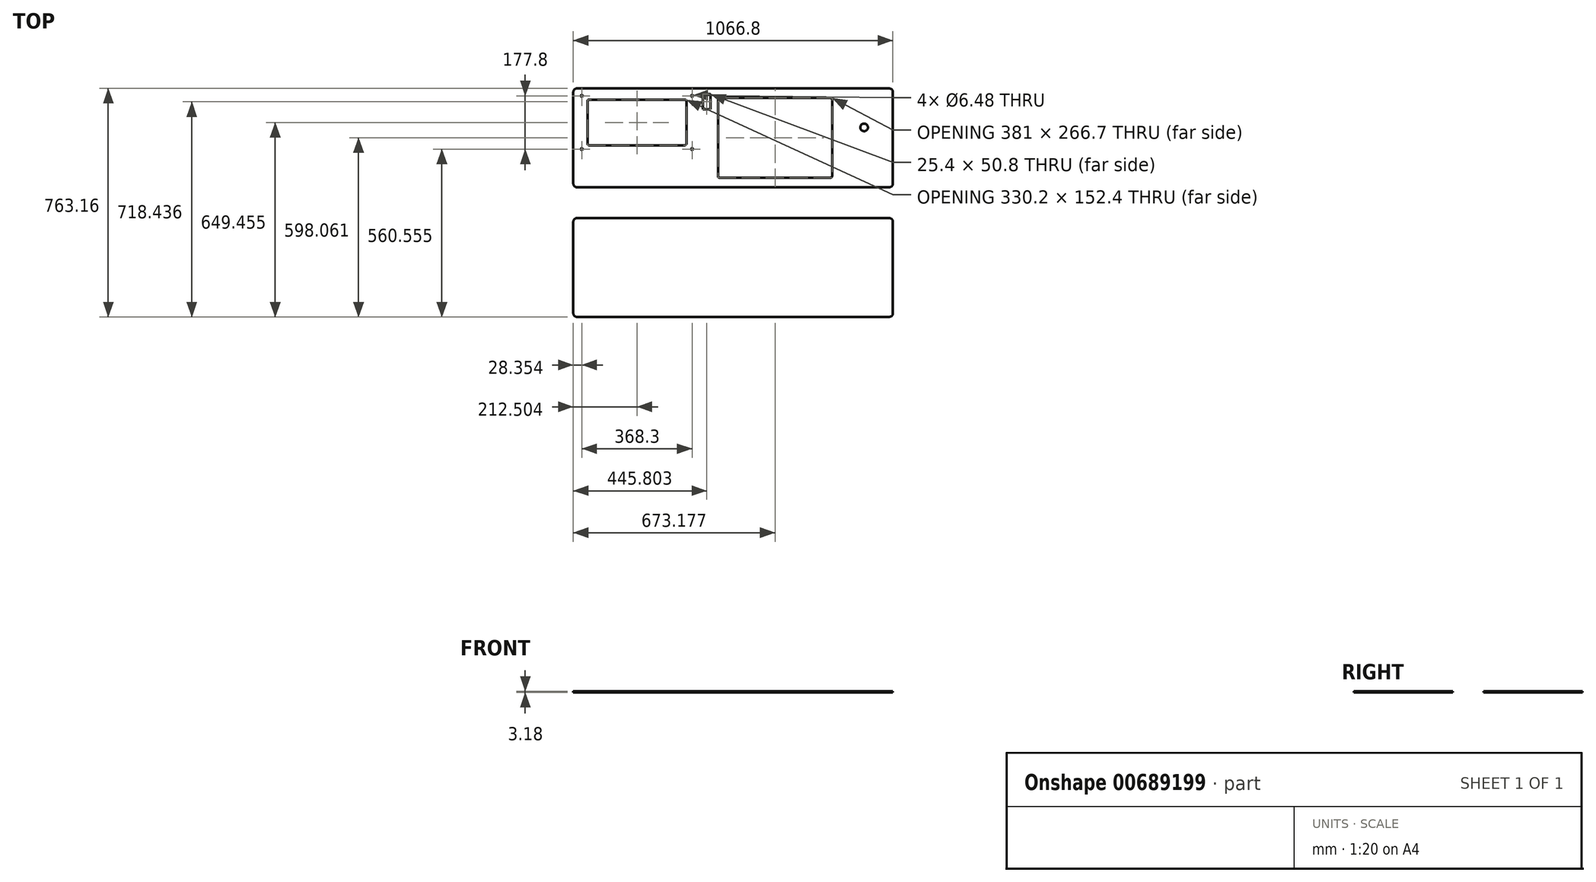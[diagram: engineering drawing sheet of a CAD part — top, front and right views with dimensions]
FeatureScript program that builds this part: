
annotation { "Feature Type Name" : "Feature", "Feature Type Description" : "" }
export const myFeature = defineFeature(function(context is Context, id is Id, definition is map)
    precondition{}
    {
        {
            var Q0;
            Q0=qCreatedBy(makeId("Top.planeOp"),FACE);
            var sketch = newSketch(context, id + "F0", { "sketchPlane" : qUnion([Q0])});
            skLineSegment(sketch, "E0.bottom", {"start": v(-578.64, 150) * mm, "end": v(488.16, 150) * mm});
            skLineSegment(sketch, "E0.top", {"start": v(-578.64, -180.2) * mm, "end": v(488.16, -180.2) * mm});
            skLineSegment(sketch, "E0.left", {"start": v(-578.64, 150) * mm, "end": v(-578.64, -180.2) * mm});
            skLineSegment(sketch, "E0.right", {"start": v(488.16, 150) * mm, "end": v(488.16, -180.2) * mm});
            skPoint(sketch, "E0.middle", {"position": v(-45.24, -15.1) * mm});
            skLineSegment(sketch, "E1.bottom", {"start": v(-95.96, -148.46) * mm, "end": v(285.04, -148.46) * mm});
            skLineSegment(sketch, "E1.top", {"start": v(-95.96, 118.24) * mm, "end": v(285.04, 118.24) * mm});
            skLineSegment(sketch, "E1.left", {"start": v(-95.96, -148.46) * mm, "end": v(-95.96, 118.24) * mm});
            skLineSegment(sketch, "E1.right", {"start": v(285.04, -148.46) * mm, "end": v(285.04, 118.24) * mm});
            skPoint(sketch, "E1.middle", {"position": v(94.54, -15.1) * mm});
            skLineSegment(sketch, "E2.bottom", {"start": v(-531.24, 112.49) * mm, "end": v(-201.04, 112.49) * mm});
            skLineSegment(sketch, "E2.top", {"start": v(-531.24, -39.91) * mm, "end": v(-201.04, -39.91) * mm});
            skLineSegment(sketch, "E2.left", {"start": v(-531.24, 112.49) * mm, "end": v(-531.24, -39.91) * mm});
            skLineSegment(sketch, "E2.right", {"start": v(-201.04, 112.49) * mm, "end": v(-201.04, -39.91) * mm});
            skPoint(sketch, "E2.middle", {"position": v(-366.14, 36.29) * mm});
            skLineSegment(sketch, "E3.bottom", {"start": v(-181.99, -52.61) * mm, "end": v(-550.29, -52.61) * mm, "construction": true});
            skLineSegment(sketch, "E3.top", {"start": v(-181.99, 125.19) * mm, "end": v(-550.29, 125.19) * mm, "construction": true});
            skLineSegment(sketch, "E3.left", {"start": v(-181.99, -52.61) * mm, "end": v(-181.99, 125.19) * mm, "construction": true});
            skLineSegment(sketch, "E3.right", {"start": v(-550.29, -52.61) * mm, "end": v(-550.29, 125.19) * mm, "construction": true});
            skCircle(sketch, "E4", {"center": v(-550.29, 125.19) * mm, "radius": 3.24 * mm});
            skCircle(sketch, "E5", {"center": v(-181.99, 125.19) * mm, "radius": 3.24 * mm});
            skCircle(sketch, "E6", {"center": v(-181.99, -52.61) * mm, "radius": 3.24 * mm});
            skCircle(sketch, "E7", {"center": v(-550.29, -52.61) * mm, "radius": 3.24 * mm});
            skCircle(sketch, "E8", {"center": v(392.03, 19.72) * mm, "radius": 12.7 * mm});
            skLineSegment(sketch, "E9.bottom", {"start": v(-145.54, 130.67) * mm, "end": v(-120.14, 130.67) * mm});
            skLineSegment(sketch, "E9.top", {"start": v(-145.54, 79.87) * mm, "end": v(-120.14, 79.87) * mm});
            skLineSegment(sketch, "E9.left", {"start": v(-145.54, 130.67) * mm, "end": v(-145.54, 79.87) * mm});
            skLineSegment(sketch, "E9.right", {"start": v(-120.14, 130.67) * mm, "end": v(-120.14, 79.87) * mm});
            skPoint(sketch, "E9.middle", {"position": v(-132.84, 105.27) * mm});
            skLineSegment(sketch, "E10", {"start": v(-578.64, -231.6) * mm, "end": v(488.16, -231.6) * mm, "construction": true});
            skLineSegment(sketch, "E11.MirrorCS", {"start": v(-578.64, -282.97) * mm, "end": v(488.16, -282.97) * mm});
            skLineSegment(sketch, "E12.MirrorCS", {"start": v(-578.64, -613.17) * mm, "end": v(-578.64, -282.97) * mm});
            skLineSegment(sketch, "E13.MirrorCS", {"start": v(-578.64, -613.17) * mm, "end": v(488.16, -613.17) * mm});
            skLineSegment(sketch, "E14.MirrorCS", {"start": v(488.16, -613.17) * mm, "end": v(488.16, -282.97) * mm});
            skSolve(sketch);
        }
        {
            var Q0;
            Q0=makeQuery(id+"F0.imprint","IMPRINT",FACE,{"disambiguationData":[TD([[makeQuery(id+"F0.imprint","IMPRINT",EDGE,{"derivedFrom":sQuery(id+"F0.wireOp",EDGE,"E0.bottom")}),-1.0]])]});
            extrude(context, id + "F1", {"entities" : qUnion([Q0]), "depth" : 3.17 * mm, "offsetDistance" : 25.4 * mm});
        }
        {
            var Q0;
            Q0=makeQuery(id+"F0.imprint","IMPRINT",FACE,{"disambiguationData":[TD([[makeQuery(id+"F0.imprint","IMPRINT",EDGE,{"derivedFrom":sQuery(id+"F0.wireOp",EDGE,"E11.MirrorCS")}),-1.0]])]});
            extrude(context, id + "F2", {"entities" : qUnion([Q0]), "depth" : 3.17 * mm, "offsetDistance" : 25.4 * mm});
        }
        {
            var Q0;
            Q0=makeQuery(id+"F1.opExtrude","SWEPT_EDGE",EDGE,{"disambiguationData":[OSD([sQuery(id+"F0.wireOp",EDGE,"E2.bottom"),sQuery(id+"F0.wireOp",EDGE,"E2.left")])]});
            var Q1;
            Q1=makeQuery(id+"F1.opExtrude","SWEPT_EDGE",EDGE,{"disambiguationData":[OSD([sQuery(id+"F0.wireOp",EDGE,"E2.top"),sQuery(id+"F0.wireOp",EDGE,"E2.left")])]});
            var Q2;
            Q2=makeQuery(id+"F1.opExtrude","SWEPT_EDGE",EDGE,{"disambiguationData":[OSD([sQuery(id+"F0.wireOp",EDGE,"E2.top"),sQuery(id+"F0.wireOp",EDGE,"E2.right")])]});
            var Q3;
            Q3=makeQuery(id+"F1.opExtrude","SWEPT_EDGE",EDGE,{"disambiguationData":[OSD([sQuery(id+"F0.wireOp",EDGE,"E2.bottom"),sQuery(id+"F0.wireOp",EDGE,"E2.right")])]});
            var Q4;
            Q4=makeQuery(id+"F1.opExtrude","SWEPT_EDGE",EDGE,{"disambiguationData":[OSD([sQuery(id+"F0.wireOp",EDGE,"E1.top"),sQuery(id+"F0.wireOp",EDGE,"E1.left")])]});
            var Q5;
            Q5=makeQuery(id+"F1.opExtrude","SWEPT_EDGE",EDGE,{"disambiguationData":[OSD([sQuery(id+"F0.wireOp",EDGE,"E1.bottom"),sQuery(id+"F0.wireOp",EDGE,"E1.left")])]});
            var Q6;
            Q6=makeQuery(id+"F1.opExtrude","SWEPT_EDGE",EDGE,{"disambiguationData":[OSD([sQuery(id+"F0.wireOp",EDGE,"E1.bottom"),sQuery(id+"F0.wireOp",EDGE,"E1.right")])]});
            var Q7;
            Q7=makeQuery(id+"F1.opExtrude","SWEPT_EDGE",EDGE,{"disambiguationData":[OSD([sQuery(id+"F0.wireOp",EDGE,"E1.top"),sQuery(id+"F0.wireOp",EDGE,"E1.right")])]});
            fillet(context, id + "F3", {"entities" : qUnion([Q0, Q1, Q2, Q3, Q4, Q5, Q6, Q7]), "radius" : 5.08 * mm, "tangentPropagation" : true, "allowEdgeOverflow" : false});
        }
        {
            var Q0;
            Q0=makeQuery(id+"F1.opExtrude","SWEPT_EDGE",EDGE,{"disambiguationData":[OSD([sQuery(id+"F0.wireOp",EDGE,"E0.bottom"),sQuery(id+"F0.wireOp",EDGE,"E0.left")])]});
            var Q1;
            Q1=makeQuery(id+"F1.opExtrude","SWEPT_EDGE",EDGE,{"disambiguationData":[OSD([sQuery(id+"F0.wireOp",EDGE,"E0.top"),sQuery(id+"F0.wireOp",EDGE,"E0.left")])]});
            var Q2;
            Q2=makeQuery(id+"F1.opExtrude","SWEPT_EDGE",EDGE,{"disambiguationData":[OSD([sQuery(id+"F0.wireOp",EDGE,"E0.top"),sQuery(id+"F0.wireOp",EDGE,"E0.right")])]});
            var Q3;
            Q3=makeQuery(id+"F1.opExtrude","SWEPT_EDGE",EDGE,{"disambiguationData":[OSD([sQuery(id+"F0.wireOp",EDGE,"E0.bottom"),sQuery(id+"F0.wireOp",EDGE,"E0.right")])]});
            var Q4;
            Q4=makeQuery(id+"F2.opExtrude","SWEPT_EDGE",EDGE,{"disambiguationData":[OSD([sQuery(id+"F0.wireOp",EDGE,"E11.MirrorCS"),sQuery(id+"F0.wireOp",EDGE,"E12.MirrorCS")])]});
            var Q5;
            Q5=makeQuery(id+"F2.opExtrude","SWEPT_EDGE",EDGE,{"disambiguationData":[OSD([sQuery(id+"F0.wireOp",EDGE,"E12.MirrorCS"),sQuery(id+"F0.wireOp",EDGE,"E13.MirrorCS")])]});
            var Q6;
            Q6=makeQuery(id+"F2.opExtrude","SWEPT_EDGE",EDGE,{"disambiguationData":[OSD([sQuery(id+"F0.wireOp",EDGE,"E13.MirrorCS"),sQuery(id+"F0.wireOp",EDGE,"E14.MirrorCS")])]});
            var Q7;
            Q7=makeQuery(id+"F2.opExtrude","SWEPT_EDGE",EDGE,{"disambiguationData":[OSD([sQuery(id+"F0.wireOp",EDGE,"E11.MirrorCS"),sQuery(id+"F0.wireOp",EDGE,"E14.MirrorCS")])]});
            fillet(context, id + "F4", {"entities" : qUnion([Q0, Q1, Q2, Q3, Q4, Q5, Q6, Q7]), "radius" : 12.7 * mm, "tangentPropagation" : true, "allowEdgeOverflow" : false});
        }
    });
